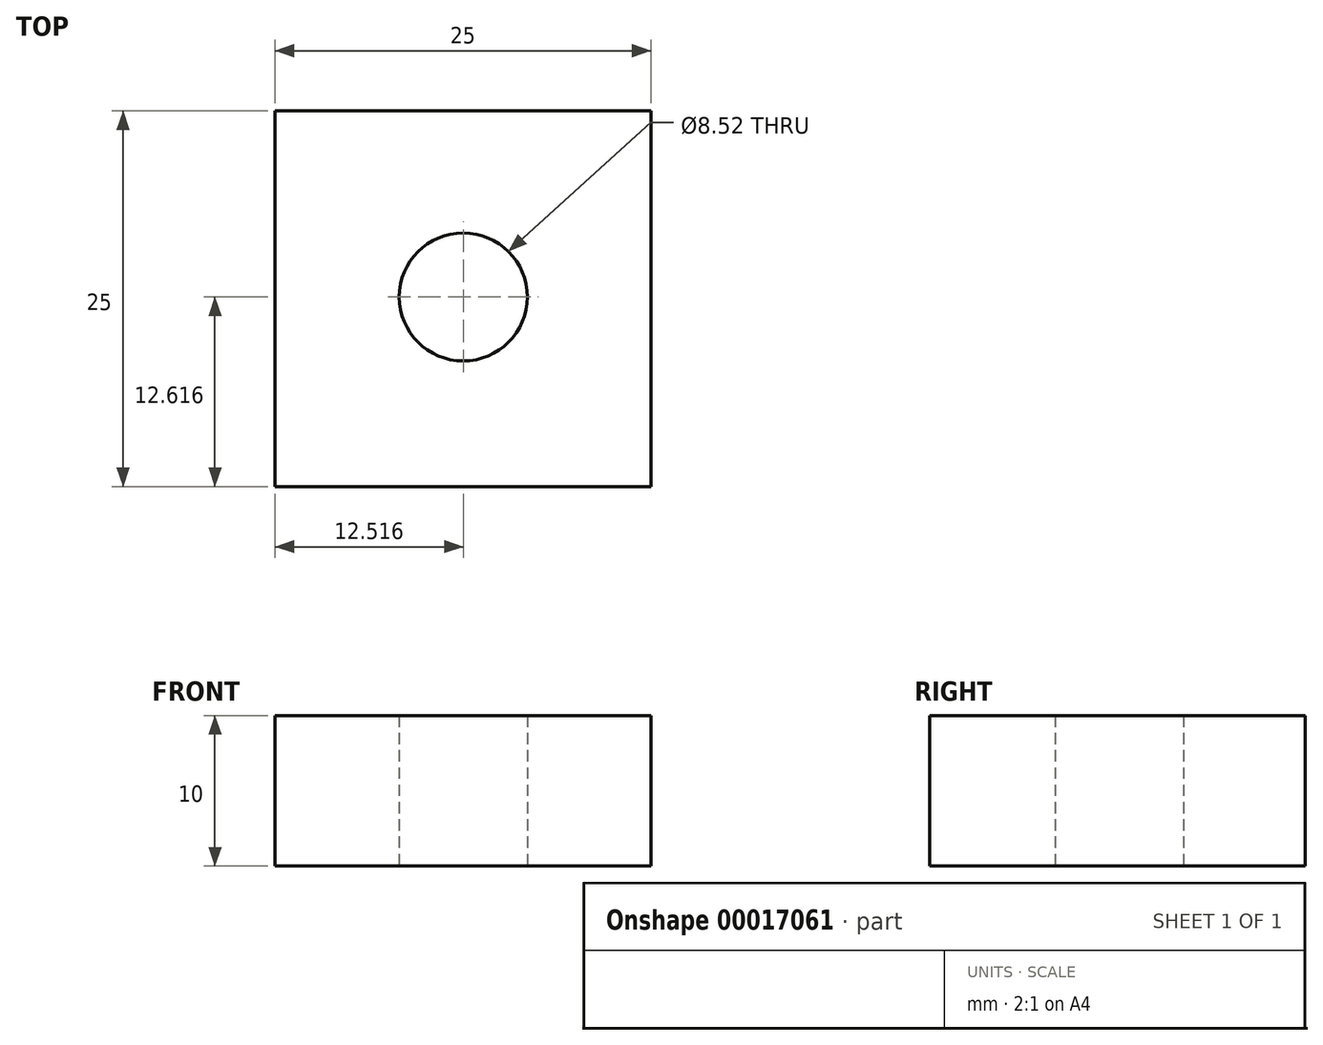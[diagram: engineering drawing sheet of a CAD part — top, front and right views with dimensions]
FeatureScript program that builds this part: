
annotation { "Feature Type Name" : "Feature", "Feature Type Description" : "" }
export const myFeature = defineFeature(function(context is Context, id is Id, definition is map)
    precondition{}
    {
        {
            var Q0;
            Q0=qCreatedBy(makeId("Top.planeOp"),FACE);
            var sketch = newSketch(context, id + "F0", { "sketchPlane" : qUnion([Q0])});
            skLineSegment(sketch, "E0.bottom", {"start": v(-3.46, 2.17) * mm, "end": v(21.54, 2.17) * mm});
            skLineSegment(sketch, "E0.top", {"start": v(-3.46, -22.83) * mm, "end": v(21.54, -22.83) * mm});
            skLineSegment(sketch, "E0.left", {"start": v(-3.46, 2.17) * mm, "end": v(-3.46, -22.83) * mm});
            skLineSegment(sketch, "E0.right", {"start": v(21.54, 2.17) * mm, "end": v(21.54, -22.83) * mm});
            skCircle(sketch, "E1", {"center": v(9.06, -10.21) * mm, "radius": 4.26 * mm});
            skLineSegment(sketch, "E2", {"start": v(-3.46, 2.17) * mm, "end": v(-3.46, -10.33) * mm});
            skLineSegment(sketch, "E3", {"start": v(-3.46, 2.17) * mm, "end": v(9.04, 2.17) * mm});
            skLineSegment(sketch, "E4", {"start": v(9.04, 2.17) * mm, "end": v(9.04, -10.21) * mm});
            skSolve(sketch);
        }
        {
            var Q0;
            Q0 = qSketchRegion(id + "F0", true);
            extrude(context, id + "F1", {"entities" : qUnion([Q0]), "depth" : 10 * mm});
        }
    });
